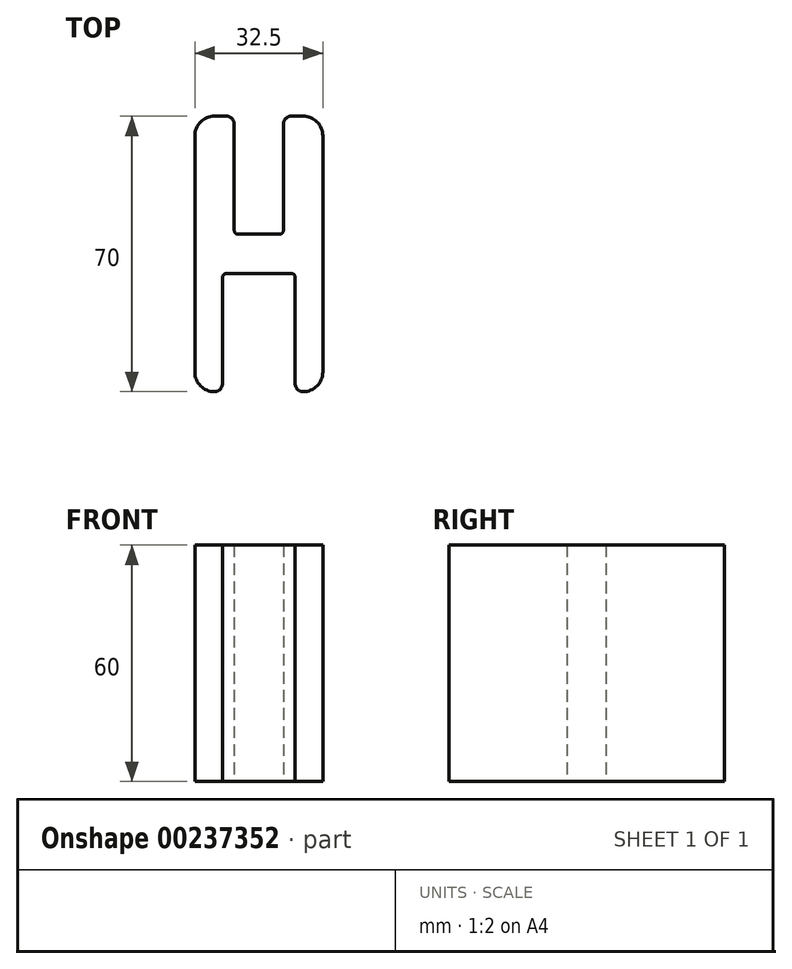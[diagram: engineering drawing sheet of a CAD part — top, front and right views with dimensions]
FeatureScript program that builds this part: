
annotation { "Feature Type Name" : "Feature", "Feature Type Description" : "" }
export const myFeature = defineFeature(function(context is Context, id is Id, definition is map)
    precondition{}
    {
        {
            var Q0;
            Q0=qCreatedBy(makeId("Top.planeOp"),FACE);
            var sketch = newSketch(context, id + "F0", { "sketchPlane" : qUnion([Q0])});
            skLineSegment(sketch, "E0", {"start": v(0, 5) * mm, "end": v(0, 65) * mm});
            skLineSegment(sketch, "E1", {"start": v(5, 70) * mm, "end": v(8, 70) * mm});
            skLineSegment(sketch, "E2", {"start": v(10, 68) * mm, "end": v(10, 41) * mm});
            skLineSegment(sketch, "E3", {"start": v(11, 40) * mm, "end": v(21.5, 40) * mm});
            skLineSegment(sketch, "E4", {"start": v(22.5, 41) * mm, "end": v(22.5, 68) * mm});
            skLineSegment(sketch, "E5", {"start": v(24.5, 70) * mm, "end": v(27.5, 70) * mm});
            skLineSegment(sketch, "E6", {"start": v(32.5, 65) * mm, "end": v(32.5, 5) * mm});
            skLineSegment(sketch, "E7", {"start": v(27.5, 0) * mm, "end": v(27.5, 0) * mm});
            skLineSegment(sketch, "E8", {"start": v(25.5, 2) * mm, "end": v(25.5, 29) * mm});
            skLineSegment(sketch, "E9", {"start": v(24.5, 30) * mm, "end": v(8, 30) * mm});
            skLineSegment(sketch, "E10", {"start": v(7, 29) * mm, "end": v(7, 2) * mm});
            skLineSegment(sketch, "E11", {"start": v(5, 0) * mm, "end": v(5, 0) * mm});
            skPoint(sketch, "E12.visualSharp", {"position": v(0, 70) * mm});
            skArc(sketch, "E12.filletArc", {"start": v(5, 70) * mm, "mid": v(1.46, 68.54) * mm, "end": v(0, 65) * mm});
            skPoint(sketch, "E13.visualSharp", {"position": v(0, 0) * mm});
            skArc(sketch, "E13.filletArc", {"start": v(0, 5) * mm, "mid": v(1.46, 1.46) * mm, "end": v(5, 0) * mm});
            skPoint(sketch, "E14.visualSharp", {"position": v(32.5, 0) * mm});
            skArc(sketch, "E14.filletArc", {"start": v(27.5, 0) * mm, "mid": v(31.04, 1.46) * mm, "end": v(32.5, 5) * mm});
            skPoint(sketch, "E15.visualSharp", {"position": v(32.5, 70) * mm});
            skArc(sketch, "E15.filletArc", {"start": v(32.5, 65) * mm, "mid": v(31.04, 68.54) * mm, "end": v(27.5, 70) * mm});
            skPoint(sketch, "E16.visualSharp", {"position": v(10, 40) * mm});
            skArc(sketch, "E16.filletArc", {"start": v(10, 41) * mm, "mid": v(10.3, 40.3) * mm, "end": v(11, 40) * mm});
            skPoint(sketch, "E17.visualSharp", {"position": v(22.5, 40) * mm});
            skArc(sketch, "E17.filletArc", {"start": v(21.5, 40) * mm, "mid": v(22.2, 40.3) * mm, "end": v(22.5, 41) * mm});
            skPoint(sketch, "E18.visualSharp", {"position": v(7, 30) * mm});
            skArc(sketch, "E18.filletArc", {"start": v(8, 30) * mm, "mid": v(7.3, 29.7) * mm, "end": v(7, 29) * mm});
            skPoint(sketch, "E19.visualSharp", {"position": v(25.5, 30) * mm});
            skArc(sketch, "E19.filletArc", {"start": v(25.5, 29) * mm, "mid": v(25.2, 29.7) * mm, "end": v(24.5, 30) * mm});
            skPoint(sketch, "E20.visualSharp", {"position": v(7, 0) * mm});
            skArc(sketch, "E20.filletArc", {"start": v(5, 0) * mm, "mid": v(6.41, 0.59) * mm, "end": v(7, 2) * mm});
            skPoint(sketch, "E21.visualSharp", {"position": v(25.5, 0) * mm});
            skArc(sketch, "E21.filletArc", {"start": v(25.5, 2) * mm, "mid": v(26.09, 0.59) * mm, "end": v(27.5, 0) * mm});
            skPoint(sketch, "E22.visualSharp", {"position": v(10, 70) * mm});
            skArc(sketch, "E22.filletArc", {"start": v(10, 68) * mm, "mid": v(9.41, 69.41) * mm, "end": v(8, 70) * mm});
            skPoint(sketch, "E23.visualSharp", {"position": v(22.5, 70) * mm});
            skArc(sketch, "E23.filletArc", {"start": v(24.5, 70) * mm, "mid": v(23.09, 69.41) * mm, "end": v(22.5, 68) * mm});
            skSolve(sketch);
        }
        {
            var Q0;
            Q0=makeQuery(id+"F0.imprint","IMPRINT",FACE,{"disambiguationData":[TD([[makeQuery(id+"F0.imprint","IMPRINT",EDGE,{"derivedFrom":sQuery(id+"F0.wireOp",EDGE,"E0")}),-1.0]])]});
            extrude(context, id + "F1", {"entities" : qUnion([Q0]), "depth" : 60 * mm});
        }
    });
